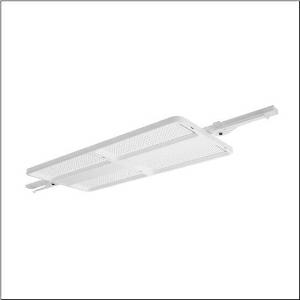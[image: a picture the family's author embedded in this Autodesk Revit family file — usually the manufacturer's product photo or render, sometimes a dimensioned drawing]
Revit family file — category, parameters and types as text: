
# Revit family: highbay_21_fur_modario_r__tragschiene_maxi_52hn11db3lma_1d5c
name_source: partatom
category: Lighting Fixtures
units: mm (PartAtom-declared; Revit-internal decimal feet)

## family parameters
Cut with Voids When Loaded = No
Host = Face
Light Source = No
Part Type = Normal
Room Calculation Point = No
Round Connector Dimension = Use Diameter
Shared = No

## types (1)
- --- (1 x LED, 3880 lm, 22.6 W, 3000K)
    Apparent Load = 23 VA
    CIE Flux Codes = 89 97 99 100 100
    Color Rendering = 80
    Color Temperature = 3000K
    Default Elevation = 1800 mm
    Description = high bay luminaire Highbay 21 for Modario® trunking rail maxi; direct symmetric narrow distribution, light control with lens of PMMA; UGR ≤ 19 (X = 4H | Y = 8H | S = 0.25H | reflection values 70/50/20); luminous flux: 25.590lm; light colour: 830, colour temperature: 3000K, MacAdam ≤ 3 SDCM (initial), colour rendering: CRI > 80; luminous efficacy: 177,7lm/W; rated service life: 75.000h (L80/B50) at AT= ta max; control: DALI 2; luminaire connection: plug, 5-pole, with phase selectionmains connection: 230..240V, AC 50/60Hz; connected load: 144W; protection rating (complete): IP64; insulation class (complete): insulation class I (protective earthing); protection symbol: D; impact resistance: IK07; certification: CE, ENEC, VDE, UKCA; internal wiring halogen-free; luminaire corresponds to IFS (International Featured Standards) requirements for safety and quality in the food industry; LABS conformity tested according to VDMA 24364:2018-05; housing frame of high-performance plastic PA6, matt traffic white (RAL 9016); cover of PMMA; fixing on rail side of steel, galvanised, white; blank cover of PC, traffic white (RAL 9016); dimension (LxWxH): 1.496 x 442 x 72mm; permissible operating ambient temperature: -40..+55°C (reducing of maximum allowable ambient temperature of 5°C with ceiling mounting); packaging unit: 1 piece
    Height = 72 mm  [stored 0.23622 ft]
    Lamp = 1 x LED
    Lamp Light Flux = 3880 lm
    Lamp Power = 22.6 W
    Lamp count = 1
    Length = 946 mm
    Luminous efficacy = 172 lm/W
    Manufacturer = Siteco
    ModVariant = No
    Model = 52HN11DB3LMA
    Mounting Place = Ceiling
    Mounting Type = Pendant
    Number of Poles = 1
    OnlyDefault = Yes
    Power Factor = 1
    Product Name = Highbay 21 für Modario® Tragschiene maxi
    Product group = high bay luminaire
    ProductGroupID = 901
    Protection Class = Protection class I
    Protection Degree = IP 64
    RLX_Detail_Level = 1
    RLX_Emergency_Light_Flux = 0 lm
    RLX_Emergency_Type = 0
    RLX_Emergency_Type_DB = No
    RlxData = <blob elided: 127625 chars, md5=383573ce>
    Socket = socket
    Standby Power = 0 W
    System Light Flux = 3880 lm
    System Power = 23 W
    Type Comments = : DC mode (central or group accumulator) initial emergency light level
    Type Image = l_1363248.jpg
    URL = http://relux.com
    VarID = @adj_000983
    Voltage = 0 V
    Weight = 0.00 kg
    Width = 442 mm

note: [stored X ft] marks values corroborated as IEEE doubles in the binary element streams (Revit-internal decimal feet)

## geometry (parser evidence)
native form markers: Blend x4, Sweep x10
no freeform markers — native parametric forms only
